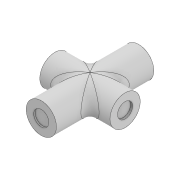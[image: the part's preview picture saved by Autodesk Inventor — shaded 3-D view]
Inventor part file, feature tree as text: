
AUTODESK INVENTOR PART (.ipt)
format: ipt  version: 2020 (Build 240168000, 168)  size: 163,328 bytes
history: native  units: mm
features: extrude x4, sketch x4, mirror x2, fillet x1, plane x1
ambient origin geometry x8: Origin, YZ Plane, XZ Plane, XY Plane, X Axis, Y Axis, Z Axis, Center Point
bodies: Solid1 (feature_tree)
feature tree (12):
  extrude  "Extrusion1"  Depth=16.1mm TaperAngle=0.0deg
  extrude  "Extrusion2"  Depth=0.25mm TaperAngle=0.0deg
  mirror  "Mirror1"
  extrude  "Extrusion3"  Depth=11.6mm TaperAngle=0.0deg
  extrude  "Extrusion4"  Depth=0.35mm TaperAngle=0.0deg
  mirror  "Mirror2"
  fillet  "Fillet1"  Radius=1.5mm
  sketch  "Sketch1"  dims[d0=5.0mm d1=16.1mm d2=0.0mm]
  sketch  "Sketch2"  dims[d3=2.5mm d4=0.25mm d5=0.0mm]
  sketch  "Sketch3"  dims[d6=5.0mm d7=11.6mm d8=0.0mm]
  sketch  "Sketch4"  dims[d9=2.5mm d10=0.35mm d11=0.0mm d12=1.5mm]
  plane  "Work Plane1"
